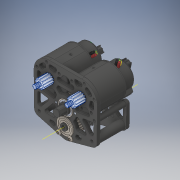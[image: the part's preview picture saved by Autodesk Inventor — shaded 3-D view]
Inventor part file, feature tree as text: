
AUTODESK INVENTOR PART (.ipt)
format: ipt  version: 2019.4 (Build 234330000, 330)  size: 6,824,960 bytes
history: native  units: in
note: dims shown in document units (in); Inventor stores cm internally (conversion verified against a paired STEP export)
features: other x36, sketch x2, projected_geometry x2, extrude x1, hole x1
ambient origin geometry x8: Origin, YZ Plane, XZ Plane, XY Plane, X Axis, Y Axis, Z Axis, Center Point
bodies: Solid1 (feature_tree), Solid2 (feature_tree), Solid3 (feature_tree), Solid4 (feature_tree), Solid5 (feature_tree), Solid6 (feature_tree), Solid7 (feature_tree), Solid8 (feature_tree), Solid9 (feature_tree), Solid10 (feature_tree), Solid11 (feature_tree), Solid12 (feature_tree), Solid13 (feature_tree), Solid14 (feature_tree), Solid15 (feature_tree), Solid16 (feature_tree), Solid17 (feature_tree), Solid18 (feature_tree), Solid19 (feature_tree), Solid20 (feature_tree), Solid21 (feature_tree), Solid22 (feature_tree), Solid23 (feature_tree), Solid24 (feature_tree), Solid25 (feature_tree), Solid26 (feature_tree), Solid27 (feature_tree), Solid28 (feature_tree), Solid29 (feature_tree), Solid30 (feature_tree), Solid31 (feature_tree), Solid32 (feature_tree), Solid33 (feature_tree), Solid34 (feature_tree), Solid35 (feature_tree), Solid36 (feature_tree)
feature tree (42):
  extrude  "Extrusion1"  [1 undecoded]
  hole  "Hole1"  [1 undecoded]
  sketch  "Sketch1"  dims[d0=2.4in d1=0.0in]
  projected_geometry  "Projected Loop1"
  sketch  "Sketch2"  dims[d2=0.196in d3=0.5in d4=0.375in d5=0.25in d6=0.5635in d7=0.75in d8=0.8108in]
  projected_geometry  "Projected Loop2"
  other  "WCP-0235-001 Rev1_1:1"
  other  "WCP-0235-002 Rev1_2:1"
  other  "12T_20dp_Falcon_Motor_217-6919_3:1"
  other  "12T_20dp_Falcon_Motor_217-6919_4:1"
  other  "60T_20dp_hex_0_500_217-3574_5:1"
  other  "thunderhex_flanged_217-4006_6:1"
  other  "BHCS_10-32_0_250_91255A261_91255A261_7:1"
  other  "22T_steel_20dp_hex_0_500_217-5463_8:1"
  other  "16T_#25_500_hex_hubbed_sprocket_217-2642_9:1"
  other  "16T_#25_500_hex_hubbed_sprocket_217-2642_10:1"
  other  "16T_#25_500_hex_hubbed_sprocket_217-2642_11:1"
  other  "375ID_875OD_flanged_217-2733_12:1"
  other  "WCP-0155-012 Rev1_13:1"
  other  "500ID_1_125OD_flanged_217_2731_14:1"
  other  "WCP-0235-003 Rev1_15:1"
  other  "26T_steel_20dp_hex_0_500_217-5466_16:1"
  other  "0_125_L_500_hex_spacer_217-2758_17:1"
  other  "BHCS_10-32_0_250_91255A261_91255A261_18:1"
  other  "WCP-0207 Rev1_19:1"
  other  "WCP-0207 Rev1_20:1"
  other  "WCP-0235-004 Rev1_21:1"
  other  "WCP-0235-004 Rev1_22:1"
  other  "217-6515_Falcon_500_Default_As Machined__23:1"
  other  "217-6515_Falcon_500_Default_As Machined__23:2"
  other  "217-6515_Falcon_500_Default_As Machined__23:3"
  other  "217-6515_Falcon_500_Default_As Machined__23:4"
  other  "217-6515_Falcon_500_Default_As Machined__23:5"
  other  "217-6515_Falcon_500_Default_As Machined__23:6"
  other  "217-6515_Falcon_500_Default_As Machined__23:7"
  other  "217-6515_Falcon_500_Default_As Machined__24:1"
  other  "217-6515_Falcon_500_Default_As Machined__24:2"
  other  "217-6515_Falcon_500_Default_As Machined__24:3"
  other  "217-6515_Falcon_500_Default_As Machined__24:4"
  other  "217-6515_Falcon_500_Default_As Machined__24:5"
  other  "217-6515_Falcon_500_Default_As Machined__24:6"
  other  "217-6515_Falcon_500_Default_As Machined__24:7"
note: 2 required parameter values undecoded (feature->parameter linkage not recoverable at this tier; creation-order binding heuristic only, values carry confidence <= 0.55)
